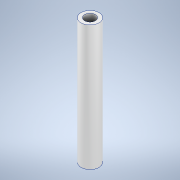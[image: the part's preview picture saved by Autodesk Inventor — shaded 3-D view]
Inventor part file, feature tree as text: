
AUTODESK INVENTOR PART (.ipt)
format: ipt  version: 2020 (Build 240168000, 168)  size: 97,280 bytes
history: native  units: in
note: dims shown in document units (in); Inventor stores cm internally (conversion verified against a paired STEP export)
features: extrude x1, sketch x1
ambient origin geometry x8: Origin, YZ Plane, XZ Plane, XY Plane, X Axis, Y Axis, Z Axis, Center Point
bodies: Solid1 (feature_tree)
feature tree (2):
  extrude  "Extrusion1"  Depth=1.378in
  sketch  "Sketch1"  dims[d0=0.1181in d1=0.1969in d2=1.378in d3=0.0in]
